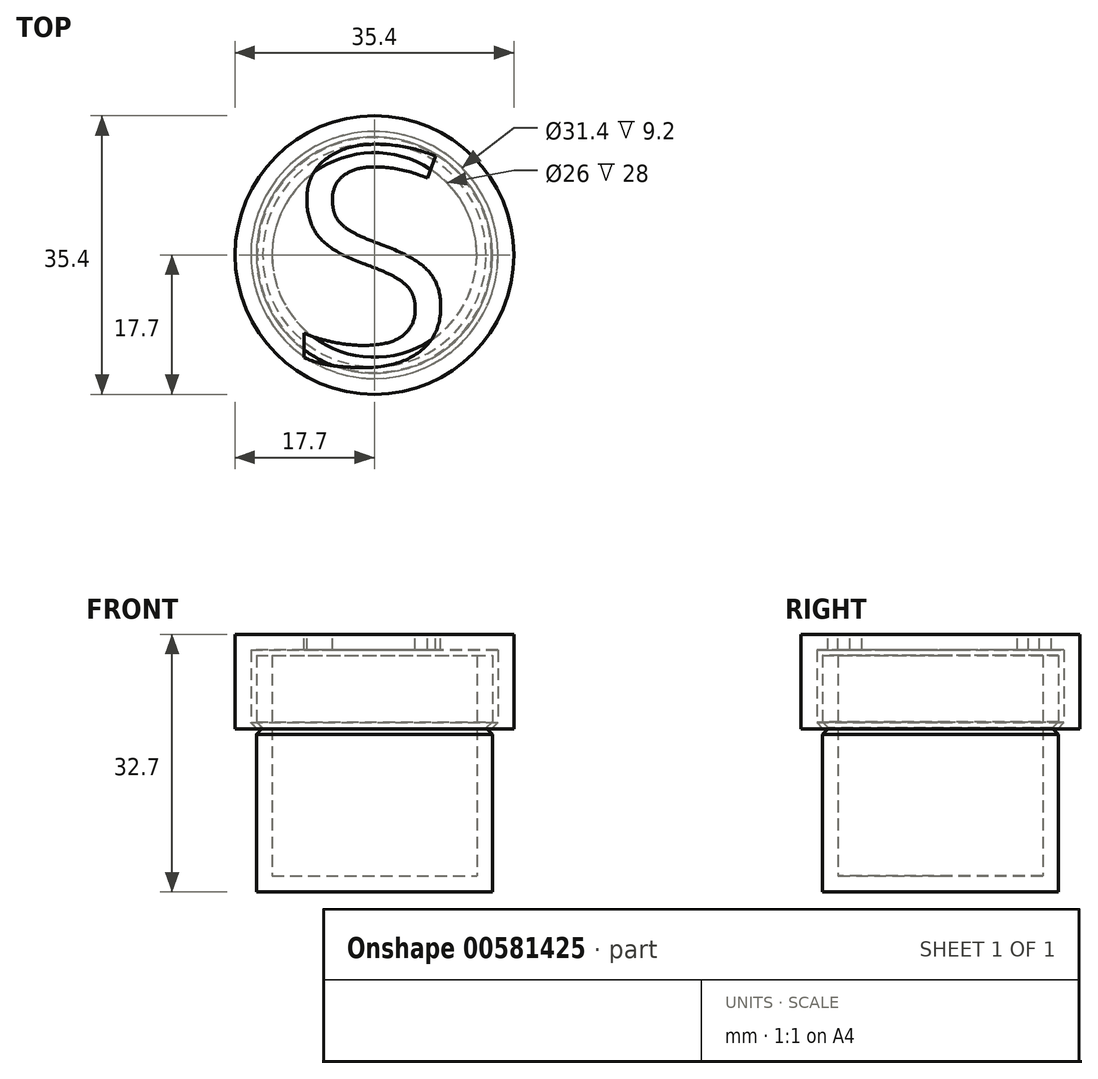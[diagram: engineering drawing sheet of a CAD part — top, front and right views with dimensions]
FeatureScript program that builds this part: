
annotation { "Feature Type Name" : "Feature", "Feature Type Description" : "" }
export const myFeature = defineFeature(function(context is Context, id is Id, definition is map)
    precondition{}
    {
        {
            var Q0;
            Q0=qCreatedBy(makeId("Front.planeOp"),FACE);
            var sketch = newSketch(context, id + "F0", { "sketchPlane" : qUnion([Q0])});
            skLineSegment(sketch, "E0", {"start": v(0, 0) * mm, "end": v(-15, 0) * mm});
            skLineSegment(sketch, "E1", {"start": v(-15, 0) * mm, "end": v(-15, 30) * mm});
            skLineSegment(sketch, "E2.0", {"start": v(-13, 2) * mm, "end": v(-13, 30) * mm});
            skLineSegment(sketch, "E2.1", {"start": v(0, 2) * mm, "end": v(-13, 2) * mm});
            skLineSegment(sketch, "E3", {"start": v(0, 2) * mm, "end": v(0, 0) * mm});
            skLineSegment(sketch, "E4", {"start": v(-15, 30) * mm, "end": v(-13, 30) * mm});
            skLineSegment(sketch, "E5", {"start": v(0, 0) * mm, "end": v(0, 45.32) * mm, "construction": true});
            skLineSegment(sketch, "E6", {"start": v(-15, 21.6) * mm, "end": v(-14.2, 20.8) * mm});
            skLineSegment(sketch, "E7", {"start": v(-14.2, 20.8) * mm, "end": v(-15, 20) * mm});
            skSolve(sketch);
        }
        {
            var Q0;
            Q0=makeQuery(id+"F0.imprint","IMPRINT",FACE,{"disambiguationData":[TD([[makeQuery(id+"F0.imprint","IMPRINT",EDGE,{"derivedFrom":sQuery(id+"F0.wireOp",EDGE,"E0")}),-1.0]])]});
            var Q1;
            Q1=sQuery(id+"F0.wireOp",EDGE,"E5");
            revolve(context, id + "F1", {"entities" : qUnion([Q0]), "axis" : qUnion([Q1]), "revolveType" : RevolveType.FULL});
        }
        {
            var Q0;
            Q0=qCreatedBy(makeId("Front.planeOp"),FACE);
            var sketch = newSketch(context, id + "F2", { "sketchPlane" : qUnion([Q0])});
            skLineSegment(sketch, "E8", {"start": v(-15, 0) * mm, "end": v(-15, 60) * mm, "construction": true});
            skLineSegment(sketch, "E9.0", {"start": v(15, 30) * mm, "end": v(-15, 30) * mm, "construction": true});
            skLineSegment(sketch, "E10", {"start": v(15, 60) * mm, "end": v(15, 0) * mm, "construction": true});
            skLineSegment(sketch, "E11.1", {"start": v(0, 30.7) * mm, "end": v(-15.7, 30.7) * mm});
            skLineSegment(sketch, "E11.2", {"start": v(-15.7, 21.5) * mm, "end": v(-15.7, 30.7) * mm});
            skLineSegment(sketch, "E12", {"start": v(-15.7, 20.7) * mm, "end": v(-17.7, 20.7) * mm});
            skLineSegment(sketch, "E13", {"start": v(-17.7, 20.7) * mm, "end": v(-17.7, 32.7) * mm});
            skLineSegment(sketch, "E14", {"start": v(-17.7, 32.7) * mm, "end": v(0, 32.7) * mm});
            skLineSegment(sketch, "E15", {"start": v(0, 32.7) * mm, "end": v(0, 30.7) * mm});
            skLineSegment(sketch, "E16", {"start": v(0, 30.7) * mm, "end": v(0, 77.47) * mm, "construction": true});
            skLineSegment(sketch, "E17", {"start": v(-15.7, 20.7) * mm, "end": v(-14.9, 20.7) * mm});
            skLineSegment(sketch, "E18", {"start": v(-14.9, 20.7) * mm, "end": v(-15.7, 21.5) * mm});
            skSolve(sketch);
        }
        {
            var Q0;
            Q0=makeQuery(id+"F2.imprint","IMPRINT",FACE,{"disambiguationData":[TD([[makeQuery(id+"F2.imprint","IMPRINT",EDGE,{"derivedFrom":sQuery(id+"F2.wireOp",EDGE,"E11.1")}),-1.0]])]});
            var Q1;
            Q1=sQuery(id+"F2.wireOp",EDGE,"E16");
            revolve(context, id + "F3", {"entities" : qUnion([Q0]), "axis" : qUnion([Q1]), "revolveType" : RevolveType.FULL});
        }
        {
            var Q0;
            Q0=makeQuery(id+"F3.opRevolve","SWEPT_FACE",FACE,{"disambiguationData":[OSD([sQuery(id+"F2.wireOp",EDGE,"E14")])]});
            var sketch = newSketch(context, id + "F4", { "sketchPlane" : qUnion([Q0])});
            skText(sketch, "E19", { "text": "S", "fontName": "OpenSans-Regular.ttf"});
            const initialGuessF4  = {"E19": [-0.01094, -0.01392, 1, 0, 0.02783]};
            skSetInitialGuess(sketch, initialGuessF4);
            skSolve(sketch);
        }
        {
            var Q0;
            Q0 = qSketchRegion(id + "F4", true);
            var Q1;
            Q1=makeQuery(id+"F3.opRevolve","SWEPT_FACE",FACE,{"disambiguationData":[OSD([sQuery(id+"F2.wireOp",EDGE,"E11.1")])]});
            extrude(context, id + "F5", {"entities" : qUnion([Q0]), "operationType" : NewBodyOperationType.REMOVE, "endBound" : BoundingType.UP_TO_SURFACE, "oppositeDirection" : true, "depth" : 25 * mm, "endBoundEntityFace" : qUnion([Q1]), "offsetDistance" : 25 * mm});
        }
    });
